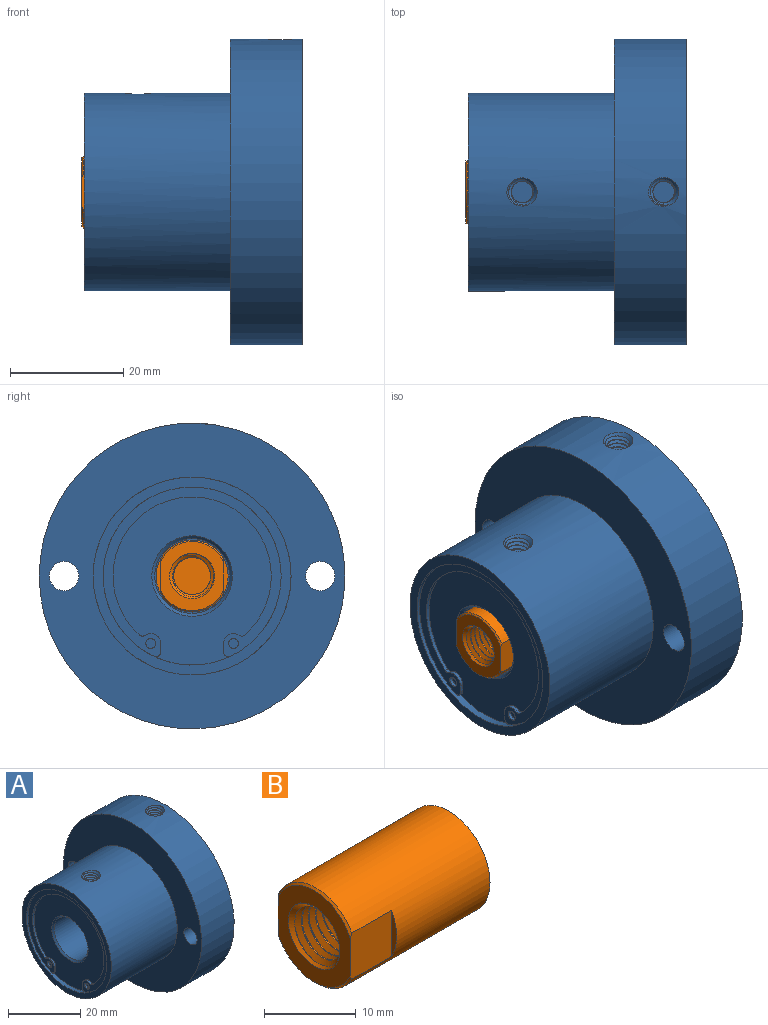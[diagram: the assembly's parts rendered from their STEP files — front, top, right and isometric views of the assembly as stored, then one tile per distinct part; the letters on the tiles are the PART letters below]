
ASSEMBLY  parts=2 mates=1
PART A: 42 faces, bbox 38.5x54x54.1 mm
  f0: cylinder r=2.41mm len=4.83mm, axis (0,0,1), area 13.2mm2, adj f1,f37,f38,f39,f41
  f1: cone r=2.67mm half-angle=45deg, axis (0,0,1), area 7.9mm2, adj f0,f2,f12,f39,f41
  f2: cone r=2.67mm half-angle=45deg, axis (0,0,1), area 0.8mm2, adj f1,f39,f40,f41
  f3: cylinder r=2.41mm len=4.83mm, axis (0,0,1), area 13.2mm2, adj f4,f32,f33,f34,f36
  f4: cone r=2.67mm half-angle=45deg, axis (0,0,1), area 8.6mm2, adj f3,f5,f15,f34,f36
  f5: cone r=2.67mm half-angle=45deg, axis (0,0,1), area 0.8mm2, adj f4,f34,f35,f36
  f6: cylinder r=0.87mm len=1.75mm, axis (1,0,0), area 3.5mm2, adj f21,f30
  f7: cylinder r=0.87mm len=1.75mm, axis (1,0,0), area 3.5mm2, adj f21,f31
  f8: cylinder r=13.97mm len=27.94mm, axis (1,0,0), area 42.7mm2, adj f16,f21,f23,f24
  f9: cone r=6.6mm half-angle=45deg, axis (-1,0,0), area 31mm2, adj f10,f16
  f10: cylinder r=6.6mm len=24.02mm, axis (-1,0,0), area 996.6mm2, adj f9,f20
  f11: cylinder r=15.72mm len=31.43mm, axis (-1,0,0), area 71.6mm2, adj f16,f19,f21,f27,f28
  f12: cylinder r=17.46mm len=34.93mm, axis (1,0,0), area 2809.6mm2, adj f1,f17,f19
  f13: cylinder r=2.58mm len=12.7mm, axis (1,0,0), area 205.8mm2, adj f17,f18
  f14: cylinder r=2.58mm len=12.7mm, axis (1,0,0), area 205.8mm2, adj f17,f18
  f15: cylinder r=26.99mm len=53.98mm, axis (1,0,0), area 2132.1mm2, adj f4,f17,f18
  f16: plane 29.69x27.94mm, normal (-1,0,0), area 465.3mm2, adj f8,f9,f11,f22,f23,f24,f25,f26
  f17: plane 53.98x53.98mm, normal (-1,0,0), area 1288.3mm2, adj f12,f13,f14,f15
  f18: plane 53.98x53.98mm, normal (1,0,0), area 2246.3mm2, adj f13,f14,f15
  f19: plane 34.93x34.93mm, normal (-1,0,0), area 182mm2, adj f11,f12
  f20: plane 13.21x13.21mm, normal (-1,0,0), area 137mm2, adj f10
  f21: plane 31.43x29.97mm, normal (-1,0,0), area 147mm2, adj f6,f7,f8,f11,f22,f23,f24,f25
  f22: cylinder r=1.75mm len=2.72mm, axis (1,0,0), area 2.4mm2, adj f16,f21,f23,f29
  f23: cylinder r=0.87mm len=1.07mm, axis (1,0,0), area 0.7mm2, adj f8,f16,f21,f22
  f24: cylinder r=0.87mm len=1.07mm, axis (1,0,0), area 0.7mm2, adj f8,f16,f21,f25
  f25: cylinder r=1.75mm len=2.72mm, axis (1,0,0), area 2.4mm2, adj f16,f21,f24,f26
  f26: plane 1.47x0.64mm, normal (0,1,0), area 0.9mm2, adj f16,f21,f25,f27
  f27: cylinder r=0.87mm len=1.25mm, axis (1,0,0), area 1.1mm2, adj f11,f16,f21,f26
  f28: cylinder r=0.87mm len=1.25mm, axis (1,0,0), area 1.1mm2, adj f11,f16,f21,f29
  f29: plane 1.47x0.64mm, normal (0,-1,0), area 0.9mm2, adj f16,f21,f22,f28
  f30: plane 1.75x1.75mm, normal (-1,0,0), area 2.4mm2, adj f6
  f31: plane 1.75x1.75mm, normal (-1,0,0), area 2.4mm2, adj f7
  f32: plane 4.83x4.83mm, normal (0,0,1), area 18.3mm2, adj f3
  f33: plane 0.69x0.52mm, normal (0,-1,0), area 0.2mm2, adj f3,f34,f35,f36
  f34: bspline ~4.83x4.83mm, area 37.7mm2, adj f3,f4,f5,f33,f35
  f35: bspline ~3.87x3.8mm, area 5.4mm2, adj f5,f33,f34,f36
  f36: bspline ~4.86x4.83mm, area 42mm2, adj f3,f4,f5,f33,f35
  f37: plane 4.83x4.83mm, normal (0,0,1), area 18.3mm2, adj f0
  f38: plane 0.69x0.52mm, normal (0,-1,0), area 0.2mm2, adj f0,f39,f40,f41
  f39: bspline ~4.83x4.83mm, area 37.7mm2, adj f0,f1,f2,f38,f40
  f40: bspline ~3.87x3.8mm, area 5.4mm2, adj f2,f38,f39,f41
  f41: bspline ~4.86x4.83mm, area 42mm2, adj f0,f1,f2,f38,f40
PART B: 16 faces, bbox 21x12.7x12.7 mm
  f0: cone r=3.97mm half-angle=45deg, axis (-1,0,0), area 11.3mm2, adj f2,f5,f8,f9,f10
  f1: cylinder r=6.35mm len=20.46mm, axis (-1,0,0), area 738.2mm2, adj f3,f4,f11,f12,f13,f14,f15
  f2: cylinder r=3.97mm len=9.53mm, axis (-1,0,0), area 39.8mm2, adj f0,f5,f6,f7,f8,f10
  f3: cone r=6.1mm half-angle=45deg, axis (1,0,0), area 4.9mm2, adj f1,f5,f12,f14
  f4: plane 12.7x12.7mm, normal (1,0,0), area 126.7mm2, adj f1
  f5: plane 12.19x11.11mm, normal (-1,0,0), area 63.6mm2, adj f0,f2,f3,f11,f12,f14
  f6: plane 7.94x7.94mm, normal (-1,0,0), area 49.5mm2, adj f2
  f7: plane 0.93x0.69mm, normal (0,-1,0), area 0.4mm2, adj f2,f8,f9,f10
  f8: bspline ~9.79x7.94mm, area 152.1mm2, adj f0,f2,f7,f9
  f9: bspline ~8.57x6.56mm, area 21.6mm2, adj f0,f7,f8,f10
  f10: bspline ~9.13x7.94mm, area 144.7mm2, adj f0,f2,f7,f9
  f11: cone r=6.1mm half-angle=45deg, axis (1,0,0), area 4.9mm2, adj f1,f5,f12,f14
  f12: plane 6.37x6.17mm, normal (0,1,0), area 38.9mm2, adj f1,f3,f5,f11,f13
  f13: plane 6.15x0.79mm, normal (-1,0,0), area 3.3mm2, adj f1,f12
  f14: plane 6.37x6.17mm, normal (0,-1,0), area 38.9mm2, adj f1,f3,f5,f11,f15
  f15: plane 6.15x0.79mm, normal (-1,0,0), area 3.3mm2, adj f1,f14
PLACE A at identity
PLACE B rot(axis=(0.33,-0.04,0.94),0deg) t=(0,0,0)mm
MATE slider B.f0 <-> A.f12  axis (-1,0,0) through (-38.89,0,0)mm
